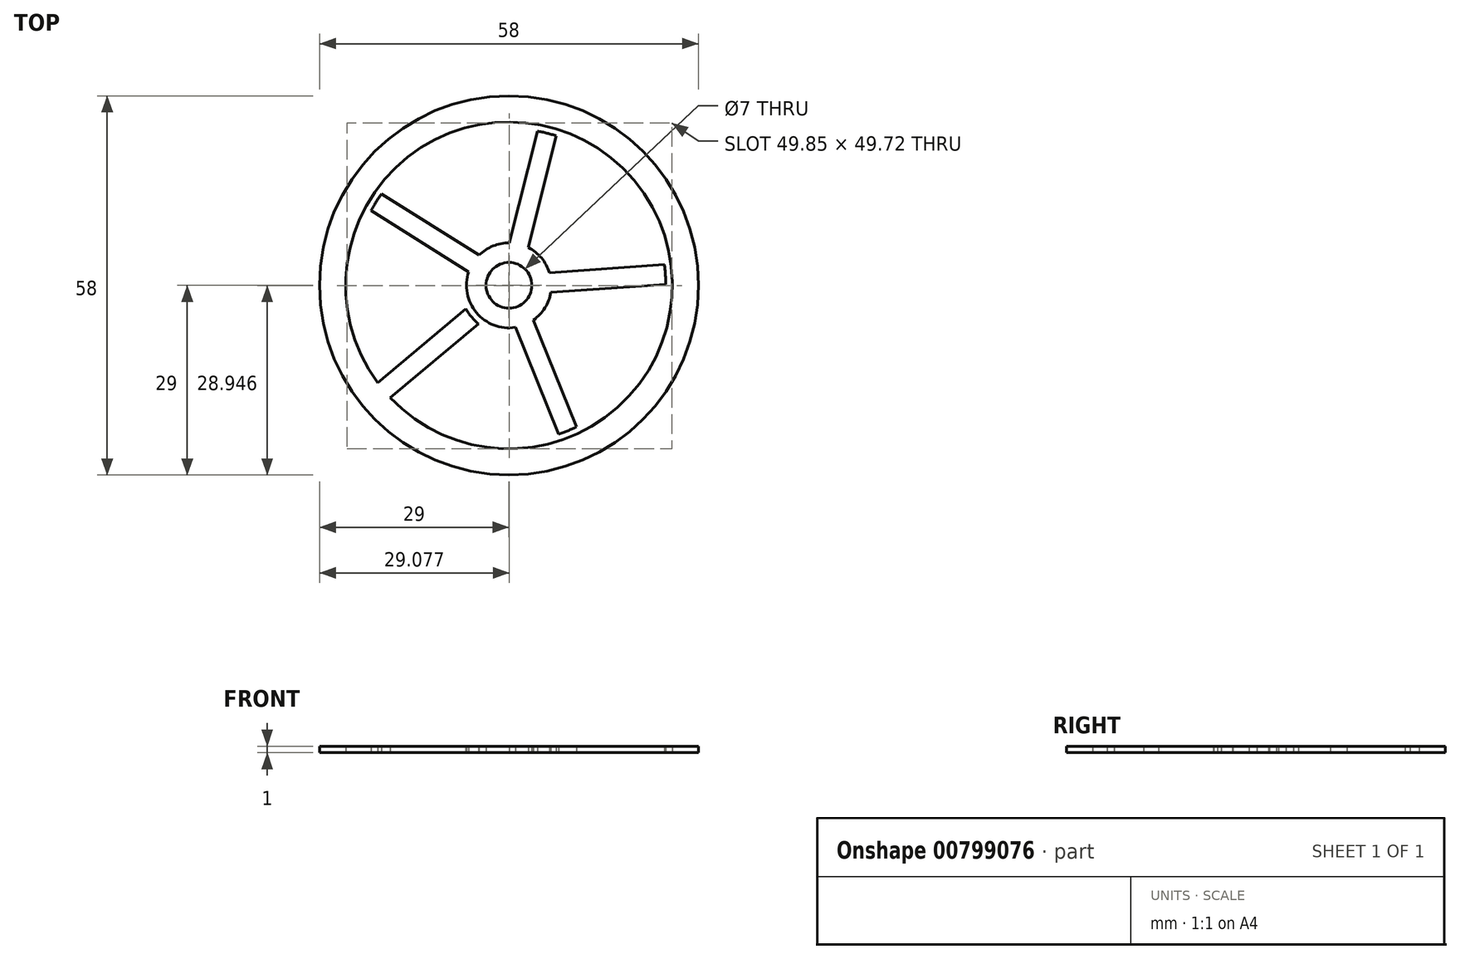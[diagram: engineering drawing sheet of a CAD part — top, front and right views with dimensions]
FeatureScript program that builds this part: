
annotation { "Feature Type Name" : "Feature", "Feature Type Description" : "" }
export const myFeature = defineFeature(function(context is Context, id is Id, definition is map)
    precondition{}
    {
        {
            var Q0;
            Q0=qCreatedBy(makeId("Top.planeOp"),FACE);
            var sketch = newSketch(context, id + "F0", { "sketchPlane" : qUnion([Q0])});
            skCircle(sketch, "E0", {"center": v(0, 0) * mm, "radius": 6.5 * mm, "construction": true});
            skCircle(sketch, "E1", {"center": v(0, 0) * mm, "radius": 25 * mm, "construction": true});
            skLineSegment(sketch, "E2", {"start": v(0, 0) * mm, "end": v(-19.15, -16.07) * mm, "construction": true});
            skLineSegment(sketch, "E3", {"start": v(-5.8, -2.92) * mm, "end": v(-20.12, -14.92) * mm, "construction": true});
            skLineSegment(sketch, "E4", {"start": v(-20.12, -14.92) * mm, "end": v(-18.19, -17.22) * mm, "construction": true});
            skLineSegment(sketch, "E5", {"start": v(-18.19, -17.22) * mm, "end": v(-3.88, -5.21) * mm, "construction": true});
            skLineSegment(sketch, "E6", {"start": v(-3.88, -5.21) * mm, "end": v(-3.1, -2.6) * mm, "construction": true});
            skLineSegment(sketch, "E7", {"start": v(-3.1, -2.6) * mm, "end": v(-5.8, -2.92) * mm, "construction": true});
            skCircle(sketch, "E8", {"center": v(0, 0) * mm, "radius": 29 * mm, "construction": true});
            skSolve(sketch);
        }
        {
            var Q0;
            Q0=qCreatedBy(makeId("Top.planeOp"),FACE);
            var sketch = newSketch(context, id + "F1", { "sketchPlane" : qUnion([Q0])});
            skLineSegment(sketch, "E9", {"start": v(-18.19, -17.22) * mm, "end": v(-3.88, -5.21) * mm});
            skLineSegment(sketch, "E10.MirrorCS", {"start": v(-20.12, -14.92) * mm, "end": v(-5.8, -2.92) * mm});
            skLineSegment(sketch, "E11", {"start": v(-20.12, -14.92) * mm, "end": v(-18.19, -17.22) * mm});
            skLineSegment(sketch, "E12", {"start": v(-3.1, -2.6) * mm, "end": v(-3.88, -5.21) * mm});
            skLineSegment(sketch, "E13", {"start": v(-5.8, -2.92) * mm, "end": v(-3.1, -2.6) * mm});
            skSolve(sketch);
        }
        {
            var Q0;
            Q0=qCreatedBy(makeId("Top.planeOp"),FACE);
            var sketch = newSketch(context, id + "F2", { "sketchPlane" : qUnion([Q0])});
            skLineSegment(sketch, "E14.bottom", {"start": v(-254, 29) * mm, "end": v(-39, 29) * mm, "construction": true});
            skLineSegment(sketch, "E14.top", {"start": v(-254, -29) * mm, "end": v(-39, -29) * mm, "construction": true});
            skLineSegment(sketch, "E14.left", {"start": v(-254, 29) * mm, "end": v(-254, -29) * mm, "construction": true});
            skLineSegment(sketch, "E14.right", {"start": v(-39, 29) * mm, "end": v(-39, -29) * mm, "construction": true});
            skLineSegment(sketch, "E15.bottom", {"start": v(-254, -17.14) * mm, "end": v(-22.22, -17.14) * mm, "construction": true});
            skLineSegment(sketch, "E15.top", {"start": v(-254, -20.14) * mm, "end": v(-22.22, -20.14) * mm, "construction": true});
            skLineSegment(sketch, "E15.left", {"start": v(-254, -17.14) * mm, "end": v(-254, -20.14) * mm, "construction": true});
            skLineSegment(sketch, "E15.right", {"start": v(-22.22, -17.14) * mm, "end": v(-22.22, -20.14) * mm, "construction": true});
            skLineSegment(sketch, "E16", {"start": v(-254, -18.64) * mm, "end": v(-22.22, -18.64) * mm, "construction": true});
            skLineSegment(sketch, "E17.bottom", {"start": v(-191, -36.5) * mm, "end": v(29, -36.5) * mm, "construction": true});
            skLineSegment(sketch, "E17.top", {"start": v(-191, -52.5) * mm, "end": v(29, -52.5) * mm, "construction": true});
            skLineSegment(sketch, "E17.left", {"start": v(-191, -36.5) * mm, "end": v(-191, -52.5) * mm, "construction": true});
            skLineSegment(sketch, "E17.right", {"start": v(29, -36.5) * mm, "end": v(29, -52.5) * mm, "construction": true});
            skLineSegment(sketch, "E18", {"start": v(-39, 0) * mm, "end": v(-29, 0) * mm, "construction": true});
            skLineSegment(sketch, "E19", {"start": v(0, -36.5) * mm, "end": v(0, -29) * mm});
            skSolve(sketch);
        }
        {
            var Q0;
            Q0=qSketchRegion(id+"F1",true);
            extrude(context, id + "F3", {"entities" : qUnion([Q0]), "depth" : 1 * mm, "offsetDistance" : 25 * mm});
        }
        {
            var Q0;
            Q0=qCreatedBy(makeId("Front.planeOp"),FACE);
            var sketch = newSketch(context, id + "F4", { "sketchPlane" : qUnion([Q0])});
            skLineSegment(sketch, "E20", {"start": v(0, 0) * mm, "end": v(0, 34.6) * mm, "construction": true});
            skSolve(sketch);
        }
        {
            var Q0;
            Q0=makeQuery(id+"F3.opExtrude","SWEPT_BODY",BODY,{"disambiguationData":[OSD([sQuery(id+"F1.wireOp",EDGE,"E9"),sQuery(id+"F1.wireOp",EDGE,"E10.MirrorCS"),sQuery(id+"F1.wireOp",EDGE,"SYlQ86mh-PDJs-R6Ng-qes8-MsBRZGDtcNO6"),sQuery(id+"F1.wireOp",EDGE,"E11")])]});
            var Q1;
            Q1=sQuery(id+"F4.wireOp",EDGE,"E20");
            circularPattern(context, id + "F5", {"operationType" : NewBodyOperationType.ADD, "entities" : qUnion([Q0]), "axis" : qUnion([Q1]), "angle" : 360 * degree, "instanceCount" : 5, "equalSpace" : true});
        }
        {
            var Q0;
            Q0=qCreatedBy(makeId("Top.planeOp"),FACE);
            var sketch = newSketch(context, id + "F6", { "sketchPlane" : qUnion([Q0])});
            skCircle(sketch, "E21", {"center": v(0, 0) * mm, "radius": 6.5 * mm});
            skSolve(sketch);
        }
        {
            var Q0;
            Q0=qCreatedBy(makeId("Top.planeOp"),FACE);
            var sketch = newSketch(context, id + "F7", { "sketchPlane" : qUnion([Q0])});
            skCircle(sketch, "E22", {"center": v(0, 0) * mm, "radius": 3.5 * mm});
            skSolve(sketch);
        }
        {
            var Q0;
            Q0=qSketchRegion(id+"F6",true);
            var Q1;
            Q1=makeQuery(id+"F6.imprint","IMPRINT",FACE,{"disambiguationData":[TD([[makeQuery(id+"F6.imprint","IMPRINT",EDGE,{"derivedFrom":sQuery(id+"F6.wireOp",EDGE,"E21")}),1.0]])]});
            extrude(context, id + "F8", {"entities" : qUnion([Q0, Q1]), "operationType" : NewBodyOperationType.ADD, "depth" : 1 * mm, "offsetDistance" : 25 * mm});
        }
        {
            var Q0;
            Q0=qSketchRegion(id+"F7",true);
            extrude(context, id + "F9", {"entities" : qUnion([Q0]), "operationType" : NewBodyOperationType.REMOVE, "endBound" : BoundingType.THROUGH_ALL, "depth" : 25 * mm, "offsetDistance" : 25 * mm});
        }
        {
            var Q0;
            Q0=qCreatedBy(makeId("Top.planeOp"),FACE);
            var sketch = newSketch(context, id + "F10", { "sketchPlane" : qUnion([Q0])});
            skCircle(sketch, "E23", {"center": v(0, 0) * mm, "radius": 25 * mm});
            skCircle(sketch, "E24", {"center": v(0, 0) * mm, "radius": 29 * mm});
            skSolve(sketch);
        }
        {
            var Q0;
            Q0=qSketchRegion(id+"F10",true);
            var Q1;
            {var subQ0=makeQuery(id+"F3.opExtrude","CAP_FACE",FACE,{"disambiguationData":[OSD([sQuery(id+"F1.wireOp",EDGE,"E9"),sQuery(id+"F1.wireOp",EDGE,"E10.MirrorCS"),sQuery(id+"F1.wireOp",EDGE,"SYlQ86mh-PDJs-R6Ng-qes8-MsBRZGDtcNO6"),sQuery(id+"F1.wireOp",EDGE,"E11")])],"isStart":false});Q1=makeQuery(id+"F8.boolean.opBoolean","MERGE",FACE,{"derivedFrom":[makeQuery(id+"F5.boolean.opBoolean","MERGE",FACE,{"derivedFrom":[subQ0,makeQuery(id+"F5.opPattern","COPY",FACE,{"derivedFrom":subQ0,"instanceName":"1"}),makeQuery(id+"F5.opPattern","COPY",FACE,{"derivedFrom":subQ0,"instanceName":"2"}),makeQuery(id+"F5.opPattern","COPY",FACE,{"derivedFrom":subQ0,"instanceName":"3"}),makeQuery(id+"F5.opPattern","COPY",FACE,{"derivedFrom":subQ0,"instanceName":"4"}),makeQuery(id+"F5.opPattern","COPY",FACE,{"derivedFrom":subQ0,"instanceName":"5"}),makeQuery(id+"F5.opPattern","COPY",FACE,{"derivedFrom":subQ0,"instanceName":"6"}),makeQuery(id+"F5.opPattern","COPY",FACE,{"derivedFrom":subQ0,"instanceName":"7"}),makeQuery(id+"F5.opPattern","COPY",FACE,{"derivedFrom":subQ0,"instanceName":"8"}),makeQuery(id+"F5.opPattern","COPY",FACE,{"derivedFrom":subQ0,"instanceName":"9"}),makeQuery(id+"F5.opPattern","COPY",FACE,{"derivedFrom":subQ0,"instanceName":"10"}),makeQuery(id+"F5.opPattern","COPY",FACE,{"derivedFrom":subQ0,"instanceName":"11"})]}),makeQuery(id+"F8.opExtrude","CAP_FACE",FACE,{"disambiguationData":[OSD([sQuery(id+"F6.wireOp",EDGE,"E21")])],"isStart":false})]});}
            extrude(context, id + "F11", {"entities" : qUnion([Q0]), "operationType" : NewBodyOperationType.ADD, "endBound" : BoundingType.UP_TO_SURFACE, "depth" : 25 * mm, "endBoundEntityFace" : qUnion([Q1]), "offsetDistance" : 25 * mm});
        }
        {
            var Q0;
            Q0=qCreatedBy(makeId("Top.planeOp"),FACE);
            var sketch = newSketch(context, id + "F12", { "sketchPlane" : qUnion([Q0])});
            skCircle(sketch, "E25", {"center": v(0, 0) * mm, "radius": 25 * mm});
            skCircle(sketch, "E26", {"center": v(0, 0) * mm, "radius": 24 * mm});
            skSolve(sketch);
        }
        {
            var Q0;
            Q0=makeQuery(id+"F12.imprint","IMPRINT",FACE,{"disambiguationData":[TD([[makeQuery(id+"F12.imprint","IMPRINT",EDGE,{"derivedFrom":sQuery(id+"F12.wireOp",EDGE,"E25")}),1.0]])]});
            extrude(context, id + "F13", {"entities" : qUnion([Q0]), "operationType" : NewBodyOperationType.REMOVE, "endBound" : BoundingType.THROUGH_ALL, "depth" : 25 * mm, "offsetDistance" : 25 * mm});
        }
        {
            var Q0;
            Q0=qCreatedBy(makeId("Top.planeOp"),FACE);
            var sketch = newSketch(context, id + "F14", { "sketchPlane" : qUnion([Q0])});
            skLineSegment(sketch, "E27.0", {"start": v(-6.22, -1.9) * mm, "end": v(-18.9, -15.57) * mm});
            skLineSegment(sketch, "E27.3", {"start": v(-15.37, -18.9) * mm, "end": v(-2.29, -6.08) * mm});
            skLineSegment(sketch, "E28", {"start": v(-18.9, -15.57) * mm, "end": v(-15.37, -18.9) * mm});
            skArc(sketch, "E29", {"start": v(-6.22, -1.9) * mm, "mid": v(-4.74, -4.45) * mm, "end": v(-2.29, -6.08) * mm});
            skSolve(sketch);
        }
        {
            var Q0;
            Q0=makeQuery(id+"F14.imprint","IMPRINT",FACE,{"disambiguationData":[TD([[makeQuery(id+"F14.imprint","IMPRINT",EDGE,{"derivedFrom":sQuery(id+"F14.wireOp",EDGE,"E27.0")}),1.0]])]});
            extrude(context, id + "F15", {"entities" : qUnion([Q0]), "operationType" : NewBodyOperationType.REMOVE, "endBound" : BoundingType.THROUGH_ALL, "depth" : 25 * mm, "offsetDistance" : 25 * mm});
        }
        {
            var Q0;
            Q0=qCreatedBy(makeId("Top.planeOp"),FACE);
            var sketch = newSketch(context, id + "F16", { "sketchPlane" : qUnion([Q0])});
            skLineSegment(sketch, "E30", {"start": v(-6.6, -3.57) * mm, "end": v(-23.15, -17.47) * mm});
            skLineSegment(sketch, "E31", {"start": v(-21.22, -19.76) * mm, "end": v(-4.67, -5.87) * mm});
            skLineSegment(sketch, "E32", {"start": v(0, 0) * mm, "end": v(-22.22, -18.64) * mm, "construction": true});
            skArc(sketch, "E33", {"start": v(-23.15, -17.47) * mm, "mid": v(-22.22, -18.64) * mm, "end": v(-21.22, -19.76) * mm});
            skCircle(sketch, "E34", {"center": v(0, 0) * mm, "radius": 4.06 * mm, "construction": true});
            skArc(sketch, "E35", {"start": v(-6.6, -3.57) * mm, "mid": v(-5.75, -4.82) * mm, "end": v(-4.67, -5.87) * mm});
            skPoint(sketch, "E36.start.orphan", {"position": v(-3.1, -2.6) * mm});
            skSolve(sketch);
        }
        {
            var Q0;
            Q0=qSketchRegion(id+"F16",true);
            var Q1;
            {var subQ0=sQuery(id+"F1.wireOp",EDGE,"E10.MirrorCS");var subQ2=sQuery(id+"F1.wireOp",EDGE,"E9");var subQ3=makeQuery(id+"F3.opExtrude","SWEPT_FACE",FACE,{"disambiguationData":[OSD([subQ2])]});var subQ4=sQuery(id+"F6.wireOp",EDGE,"E21");var subQ5=sQuery(id+"F1.wireOp",EDGE,"E11");var subQ6=sQuery(id+"F1.wireOp",EDGE,"SYlQ86mh-PDJs-R6Ng-qes8-MsBRZGDtcNO6");var subQ7=makeQuery(id+"F3.opExtrude","CAP_FACE",FACE,{"disambiguationData":[OSD([subQ2,subQ0,subQ6,subQ5])],"isStart":false});Q1=makeQuery(id+"F13.boolean.opBoolean","SPLIT",FACE,{"disambiguationData":[TD([subQ3])],"derivedFrom":makeQuery(id+"F11.boolean.opBoolean","MERGE",FACE,{"derivedFrom":[makeQuery(id+"F8.boolean.opBoolean","MERGE",FACE,{"derivedFrom":[makeQuery(id+"F5.boolean.opBoolean","MERGE",FACE,{"derivedFrom":[subQ7,makeQuery(id+"F5.opPattern","COPY",FACE,{"derivedFrom":subQ7,"instanceName":"1"}),makeQuery(id+"F5.opPattern","COPY",FACE,{"derivedFrom":subQ7,"instanceName":"2"}),makeQuery(id+"F5.opPattern","COPY",FACE,{"derivedFrom":subQ7,"instanceName":"3"}),makeQuery(id+"F5.opPattern","COPY",FACE,{"derivedFrom":subQ7,"instanceName":"4"}),makeQuery(id+"F5.opPattern","COPY",FACE,{"derivedFrom":subQ7,"instanceName":"5"}),makeQuery(id+"F5.opPattern","COPY",FACE,{"derivedFrom":subQ7,"instanceName":"6"}),makeQuery(id+"F5.opPattern","COPY",FACE,{"derivedFrom":subQ7,"instanceName":"7"}),makeQuery(id+"F5.opPattern","COPY",FACE,{"derivedFrom":subQ7,"instanceName":"8"}),makeQuery(id+"F5.opPattern","COPY",FACE,{"derivedFrom":subQ7,"instanceName":"9"}),makeQuery(id+"F5.opPattern","COPY",FACE,{"derivedFrom":subQ7,"instanceName":"10"}),makeQuery(id+"F5.opPattern","COPY",FACE,{"derivedFrom":subQ7,"instanceName":"11"})]}),makeQuery(id+"F8.opExtrude","CAP_FACE",FACE,{"disambiguationData":[OSD([subQ4])],"isStart":false})]}),makeQuery(id+"F11.opExtrude","CAP_FACE",FACE,{"disambiguationData":[OSD([subQ2,subQ0,subQ6,subQ5,subQ4])],"isStart":false})]})});}
            extrude(context, id + "F17", {"entities" : qUnion([Q0]), "operationType" : NewBodyOperationType.ADD, "endBound" : BoundingType.UP_TO_SURFACE, "depth" : 25 * mm, "endBoundEntityFace" : qUnion([Q1]), "offsetDistance" : 25 * mm});
        }
    });
